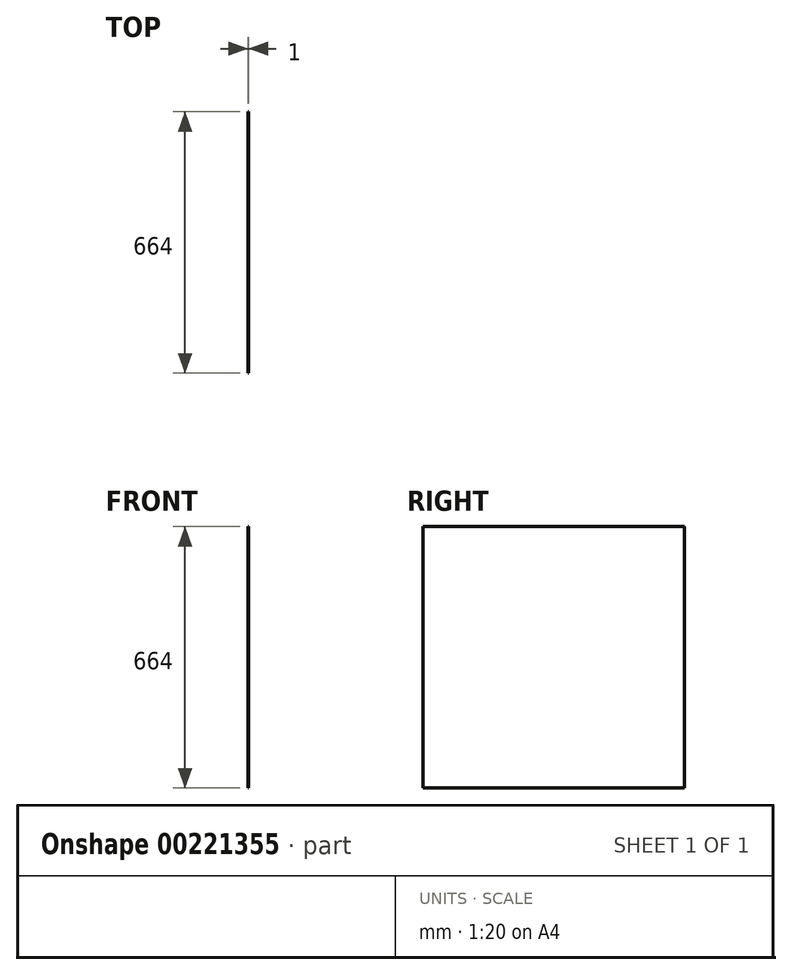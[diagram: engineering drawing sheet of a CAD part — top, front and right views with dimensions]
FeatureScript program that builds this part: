
annotation { "Feature Type Name" : "Feature", "Feature Type Description" : "" }
export const myFeature = defineFeature(function(context is Context, id is Id, definition is map)
    precondition{}
    {
        {
            var Q0;
            Q0=qCreatedBy(makeId("Right.planeOp"),FACE);
            var sketch = newSketch(context, id + "F0", { "sketchPlane" : qUnion([Q0])});
            skLineSegment(sketch, "E0.bottom", {"start": v(332, 318.91) * mm, "end": v(-332, 318.91) * mm});
            skLineSegment(sketch, "E0.top", {"start": v(332, -345.09) * mm, "end": v(-332, -345.09) * mm});
            skLineSegment(sketch, "E0.left", {"start": v(332, 318.91) * mm, "end": v(332, -345.09) * mm});
            skLineSegment(sketch, "E0.right", {"start": v(-332, 318.91) * mm, "end": v(-332, -345.09) * mm});
            skPoint(sketch, "E0.middle", {"position": v(0, -13.09) * mm});
            skSolve(sketch);
        }
        {
            var Q0;
            Q0 = qSketchRegion(id + "F0", true);
            extrude(context, id + "F1", {"entities" : qUnion([Q0]), "depth" : 1 * mm});
        }
    });
